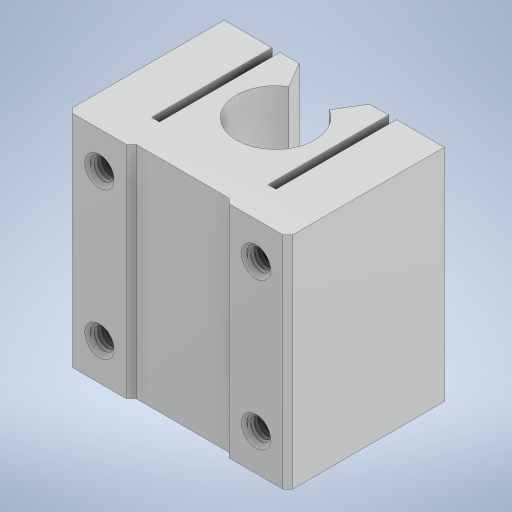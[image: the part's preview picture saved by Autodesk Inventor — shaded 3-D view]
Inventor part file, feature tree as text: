
AUTODESK INVENTOR PART (.ipt)
format: ipt  version: 2024 (Build 280153000, 153)  size: 2,503,168 bytes
history: native  units: in
note: dims shown in document units (in); Inventor stores cm internally (conversion verified against a paired STEP export)
features: extrude x4, sketch x4, projected_geometry x1, other x1
ambient origin geometry x8: Origin, YZ Plane, XZ Plane, XY Plane, X Axis, Y Axis, Z Axis, Center Point
bodies: Solid4 (feature_tree)
feature tree (10):
  extrude  "Extrusion1"  Depth=0.6299in
  extrude  "Extrusion2"  Depth=0.3937in TaperAngle=0.0deg
  extrude  "Extrusion3"  [1 undecoded]
  extrude  "Extrusion4"  [1 undecoded]
  sketch  "Sketch1"  dims[d0=3.937in d1=0.0in d2=0.6299in]
  sketch  "Sketch2"  dims[d3=0.3937in d4=0.0in d5=0.3937in d6=0.0in]
  sketch  "Sketch3"  dims[d7=0.3937in d8=0.0in]
  projected_geometry  "Projected Loop1"
  sketch  "Sketch4"
  other  "Guide support"
note: 2 required parameter values undecoded (feature->parameter linkage not recoverable at this tier; creation-order binding heuristic only, values carry confidence <= 0.55)
